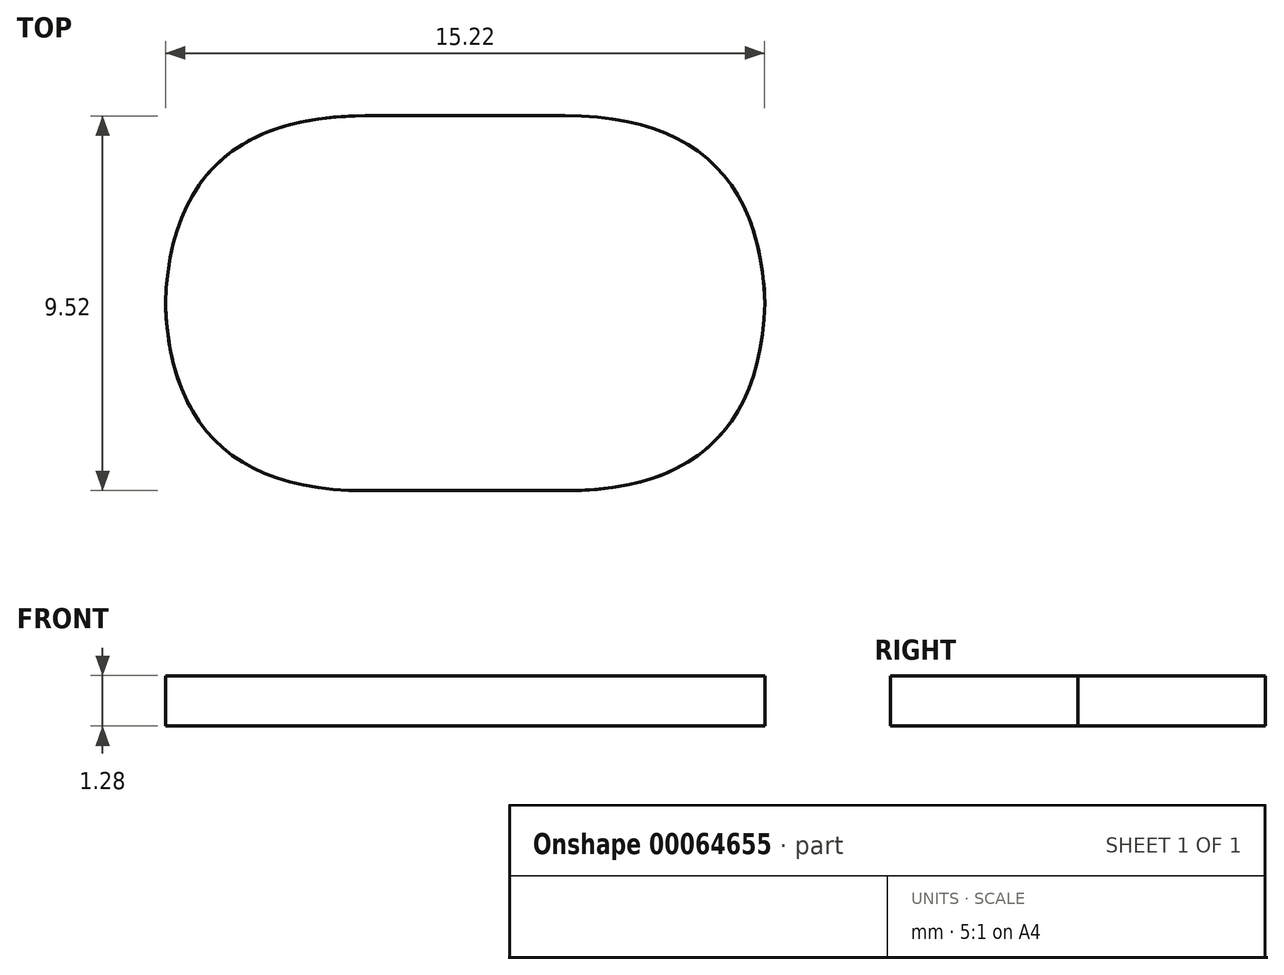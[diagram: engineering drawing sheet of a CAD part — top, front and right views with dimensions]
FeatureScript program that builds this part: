
annotation { "Feature Type Name" : "Feature", "Feature Type Description" : "" }
export const myFeature = defineFeature(function(context is Context, id is Id, definition is map)
    precondition{}
    {
        {
            var Q0;
            Q0=qCreatedBy(makeId("Top.planeOp"),FACE);
            var sketch = newSketch(context, id + "F0", { "sketchPlane" : qUnion([Q0])});
            skLineSegment(sketch, "E0.rect.bottom", {"start": v(7.62, -4.76) * mm, "end": v(-7.62, -4.76) * mm});
            skLineSegment(sketch, "E0.rect.top", {"start": v(7.62, 4.76) * mm, "end": v(-7.62, 4.76) * mm});
            skLineSegment(sketch, "E0.rect.left", {"start": v(7.62, -4.76) * mm, "end": v(7.62, 4.76) * mm});
            skLineSegment(sketch, "E0.rect.right", {"start": v(-7.62, -4.76) * mm, "end": v(-7.62, 4.76) * mm});
            skPoint(sketch, "E0.rect.middle", {"position": v(0, 0) * mm});
            skSolve(sketch);
        }
        {
            var Q0;
            Q0=makeQuery(id+"F0.imprint","IMPRINT",FACE,{"disambiguationData":[TD([[makeQuery(id+"F0.imprint","IMPRINT",EDGE,{"derivedFrom":sQuery(id+"F0.wireOp",EDGE,"E0.rect.bottom")}),-1.0]])]});
            extrude(context, id + "F1", {"entities" : qUnion([Q0]), "depth" : 0.64 * mm, "hasSecondDirection" : true, "secondDirectionOppositeDirection" : true, "secondDirectionDepth" : 0.64 * mm});
        }
        {
            var Q0;
            Q0=makeQuery(id+"F1.opExtrude","SWEPT_EDGE",EDGE,{"disambiguationData":[OSD([sQuery(id+"F0.wireOp",EDGE,"E0.rect.bottom"),sQuery(id+"F0.wireOp",EDGE,"E0.rect.right")])]});
            var Q1;
            Q1=makeQuery(id+"F1.opExtrude","SWEPT_EDGE",EDGE,{"disambiguationData":[OSD([sQuery(id+"F0.wireOp",EDGE,"E0.rect.bottom"),sQuery(id+"F0.wireOp",EDGE,"E0.rect.left")])]});
            var Q2;
            Q2=makeQuery(id+"F1.opExtrude","SWEPT_EDGE",EDGE,{"disambiguationData":[OSD([sQuery(id+"F0.wireOp",EDGE,"E0.rect.top"),sQuery(id+"F0.wireOp",EDGE,"E0.rect.left")])]});
            var Q3;
            Q3=makeQuery(id+"F1.opExtrude","SWEPT_EDGE",EDGE,{"disambiguationData":[OSD([sQuery(id+"F0.wireOp",EDGE,"E0.rect.top"),sQuery(id+"F0.wireOp",EDGE,"E0.rect.right")])]});
            fillet(context, id + "F2", {"entities" : qUnion([Q0, Q1, Q2, Q3]), "radius" : 5.08 * mm, "tangentPropagation" : true, "rho" : 0.5, "crossSection" : FilletCrossSection.CONIC, "allowEdgeOverflow" : false});
        }
    });
